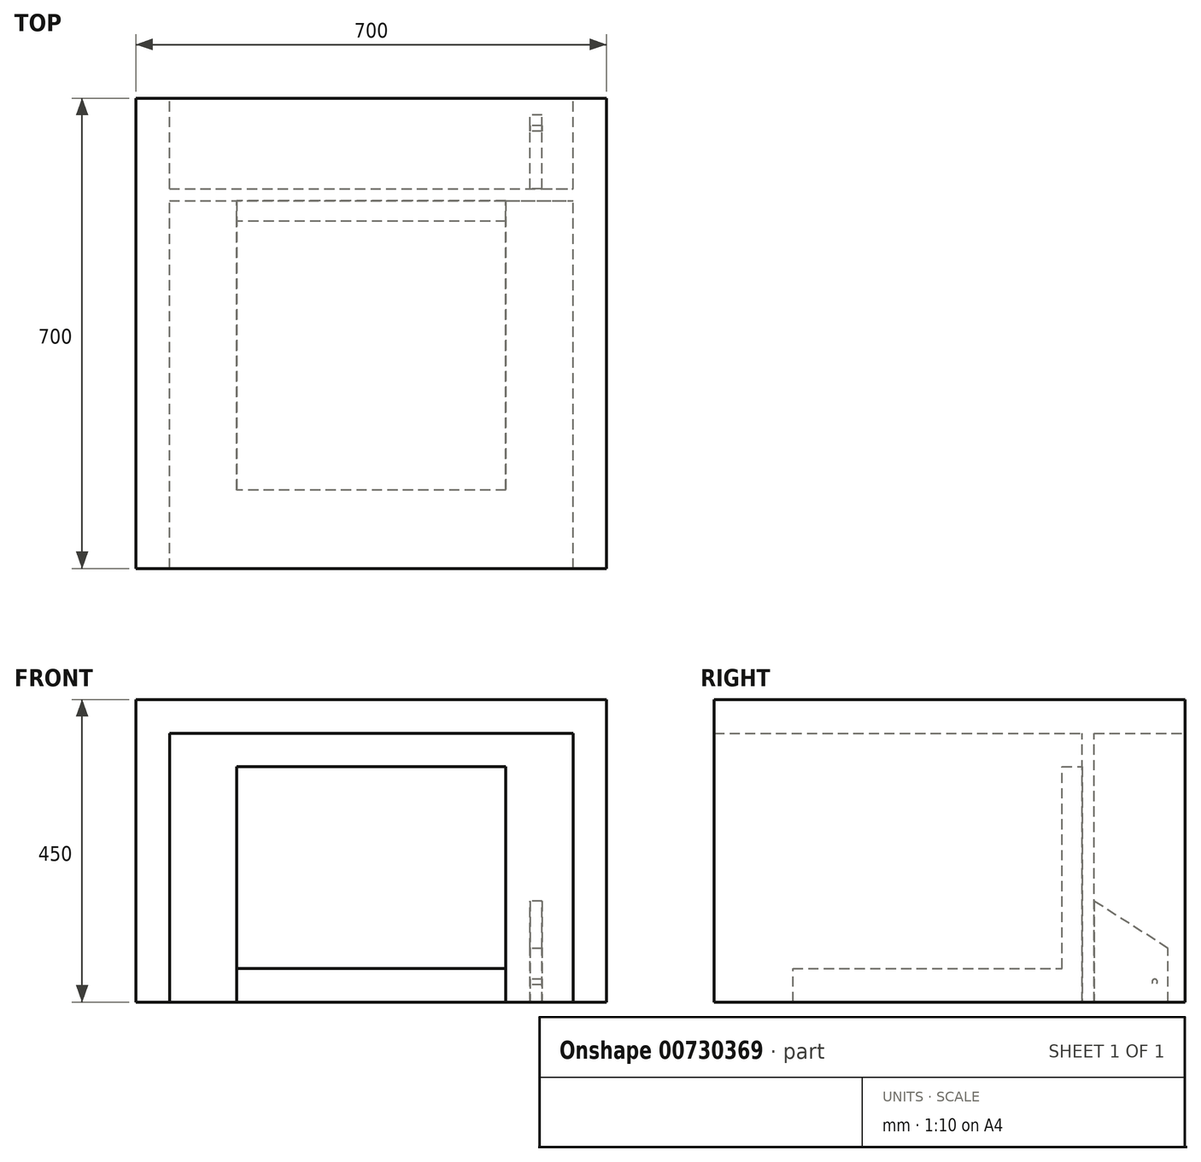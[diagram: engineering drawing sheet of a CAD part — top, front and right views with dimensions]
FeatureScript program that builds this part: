
annotation { "Feature Type Name" : "Feature", "Feature Type Description" : "" }
export const myFeature = defineFeature(function(context is Context, id is Id, definition is map)
    precondition{}
    {
        {
            var Q0;
            Q0=qCreatedBy(makeId("Front.planeOp"),FACE);
            var sketch = newSketch(context, id + "F0", { "sketchPlane" : qUnion([Q0])});
            skLineSegment(sketch, "E0", {"start": v(-300, 0) * mm, "end": v(-350, 0) * mm});
            skLineSegment(sketch, "E1", {"start": v(-350, 0) * mm, "end": v(-350, 450) * mm});
            skLineSegment(sketch, "E2", {"start": v(-350, 450) * mm, "end": v(350, 450) * mm});
            skLineSegment(sketch, "E3", {"start": v(350, 450) * mm, "end": v(350, 0) * mm});
            skLineSegment(sketch, "E4", {"start": v(350, 0) * mm, "end": v(300, 0) * mm});
            skLineSegment(sketch, "E5", {"start": v(300, 0) * mm, "end": v(300, 400) * mm});
            skLineSegment(sketch, "E6", {"start": v(300, 400) * mm, "end": v(-300, 400) * mm});
            skLineSegment(sketch, "E7", {"start": v(-300, 400) * mm, "end": v(-300, 0) * mm});
            skSolve(sketch);
        }
        {
            var Q0;
            Q0 = qSketchRegion(id + "F0", true);
            extrude(context, id + "F1", {"entities" : qUnion([Q0]), "depth" : 700 * mm, "offsetDistance" : 25 * mm});
        }
        {
            var Q0;
            Q0=makeQuery(id+"F1.opExtrude","SWEPT_FACE",FACE,{"disambiguationData":[OSD([sQuery(id+"F0.wireOp",EDGE,"E6")])]});
            var sketch = newSketch(context, id + "F2", { "sketchPlane" : qUnion([Q0])});
            skLineSegment(sketch, "E8.bottom", {"start": v(-300, 135) * mm, "end": v(300, 135) * mm});
            skLineSegment(sketch, "E8.top", {"start": v(-300, 153) * mm, "end": v(300, 153) * mm});
            skLineSegment(sketch, "E8.left", {"start": v(-300, 135) * mm, "end": v(-300, 153) * mm});
            skLineSegment(sketch, "E8.right", {"start": v(300, 135) * mm, "end": v(300, 153) * mm});
            skSolve(sketch);
        }
        {
            var Q0;
            Q0 = qSketchRegion(id + "F2", true);
            extrude(context, id + "F3", {"entities" : qUnion([Q0]), "operationType" : NewBodyOperationType.ADD, "depth" : 400 * mm, "offsetDistance" : 25 * mm});
        }
        {
            var Q0;
            {var subQ2=sQuery(id+"F0.wireOp",EDGE,"E5");var subQ4=sQuery(id+"F2.wireOp",EDGE,"E8.bottom");Q0=makeQuery(id+"F3.boolean.opBoolean","SPLIT",FACE,{"disambiguationData":[TD([makeQuery(id+"F3.opExtrude","SWEPT_FACE",FACE,{"disambiguationData":[OSD([subQ4])]})])],"derivedFrom":makeQuery(id+"F1.opExtrude","SWEPT_FACE",FACE,{"disambiguationData":[OSD([subQ2])]})});}
            var sketch = newSketch(context, id + "F4", { "sketchPlane" : qUnion([Q0])});
            skCircle(sketch, "E9", {"center": v(15, 10) * mm, "radius": 5 * mm});
            skSolve(sketch);
        }
        {
            var Q0;
            Q0=qCreatedBy(makeId("Right.planeOp"),FACE);
            var sketch = newSketch(context, id + "F5", { "sketchPlane" : qUnion([Q0])});
            skLineSegment(sketch, "E10", {"start": v(-135, 0) * mm, "end": v(-25, 0) * mm});
            skLineSegment(sketch, "E11", {"start": v(-25, 0) * mm, "end": v(-25, 80) * mm});
            skLineSegment(sketch, "E12", {"start": v(-25, 80) * mm, "end": v(-135, 150) * mm});
            skLineSegment(sketch, "E13", {"start": v(-135, 150) * mm, "end": v(-135, 0) * mm});
            skCircle(sketch, "E14", {"center": v(-45, 30) * mm, "radius": 4 * mm});
            skSolve(sketch);
        }
        {
            var Q0;
            Q0=makeQuery(id+"F5.imprint","IMPRINT",FACE,{"disambiguationData":[TD([[makeQuery(id+"F5.imprint","IMPRINT",EDGE,{"derivedFrom":sQuery(id+"F5.wireOp",EDGE,"E10")}),1.0]])]});
            extrude(context, id + "F6", {"entities" : qUnion([Q0]), "operationType" : NewBodyOperationType.ADD, "depth" : (236 + 18) * mm, "offsetDistance" : 25 * mm, "hasSecondDirection" : true, "secondDirectionOppositeDirection" : false, "secondDirectionDepth" : 236 * mm});
        }
        {
            var Q0;
            Q0=qCreatedBy(makeId("Right.planeOp"),FACE);
            var sketch = newSketch(context, id + "F7", { "sketchPlane" : qUnion([Q0])});
            skLineSegment(sketch, "E15", {"start": v(-583, 0) * mm, "end": v(-583, 50) * mm});
            skLineSegment(sketch, "E16", {"start": v(-583, 50) * mm, "end": v(-183, 50) * mm});
            skLineSegment(sketch, "E17", {"start": v(-183, 50) * mm, "end": v(-183, 350) * mm});
            skLineSegment(sketch, "E18", {"start": v(-183, 350) * mm, "end": v(-153, 350) * mm});
            skLineSegment(sketch, "E19", {"start": v(-153, 350) * mm, "end": v(-153, 0) * mm});
            skLineSegment(sketch, "E20", {"start": v(-153, 0) * mm, "end": v(-583, 0) * mm});
            skSolve(sketch);
        }
        {
            var Q0;
            Q0 = qSketchRegion(id + "F7", true);
            extrude(context, id + "F8", {"entities" : qUnion([Q0]), "operationType" : NewBodyOperationType.ADD, "depth" : 400 * mm, "offsetDistance" : 25 * mm, "symmetric" : true});
        }
    });
